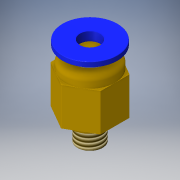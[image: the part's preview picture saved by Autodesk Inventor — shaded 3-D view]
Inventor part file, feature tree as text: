
AUTODESK INVENTOR PART (.ipt)
format: ipt  version: 2016 SP1 (Build 200210100, 210)  size: 208,384 bytes
history: native  units: mm
features: sketch x7, extrude x5, fillet x3, revolve x1, thread x1, hole x1
ambient origin geometry x8: Origin, YZ Plane, XZ Plane, XY Plane, X Axis, Y Axis, Z Axis, Center Point
bodies: Solid1 (feature_tree)
feature tree (18):
  revolve  "Revolution1"  [1 undecoded]
  thread  "Thread1"  [1 undecoded]
  extrude  "Extrusion1"  Depth=10.0mm TaperAngle=0.0deg
  extrude  "Extrusion2"  Depth=7.5mm TaperAngle=0.0deg
  fillet  "Fillet1"  Radius=10.0mm
  extrude  "Extrusion3"  Depth=1.5mm
  extrude  "Extrusion4"  Depth=1.5mm TaperAngle=0.0deg
  hole  "Hole1"  [1 undecoded]
  fillet  "Fillet2"  Radius=0.1mm
  fillet  "Fillet3"  Radius=0.2mm
  extrude  "Extrusion5"  Depth=0.75mm TaperAngle=0.0deg
  sketch  "Sketch1"  dims[d0=2.5mm d1=4.0mm d2=1.5mm]
  sketch  "Sketch2"  dims[d6=90.0deg d7=10.0mm d8=0.0mm]
  sketch  "Sketch3"  dims[d9=10.0mm d10=7.5mm d11=0.0mm d12=10.0mm]
  sketch  "Sketch4"  dims[d13=2.5mm d14=0.0mm d15=1.5mm]
  sketch  "Sketch5"  dims[d16=5.0mm d17=1.5mm d18=0.0mm]
  sketch  "Sketch6"  dims[d19=11.0mm d20=1.0mm d21=0.0mm]
  sketch  "Sketch7"  dims[d22=4.0mm d23=6.0mm d24=4.0mm d25=2.0mm d26=90.0deg d27=8.0mm d28=20.594885mm d29=0.1mm d30=0.2mm d31=0.75mm d32=0.0mm]
note: 3 required parameter values undecoded (feature->parameter linkage not recoverable at this tier; creation-order binding heuristic only, values carry confidence <= 0.55)